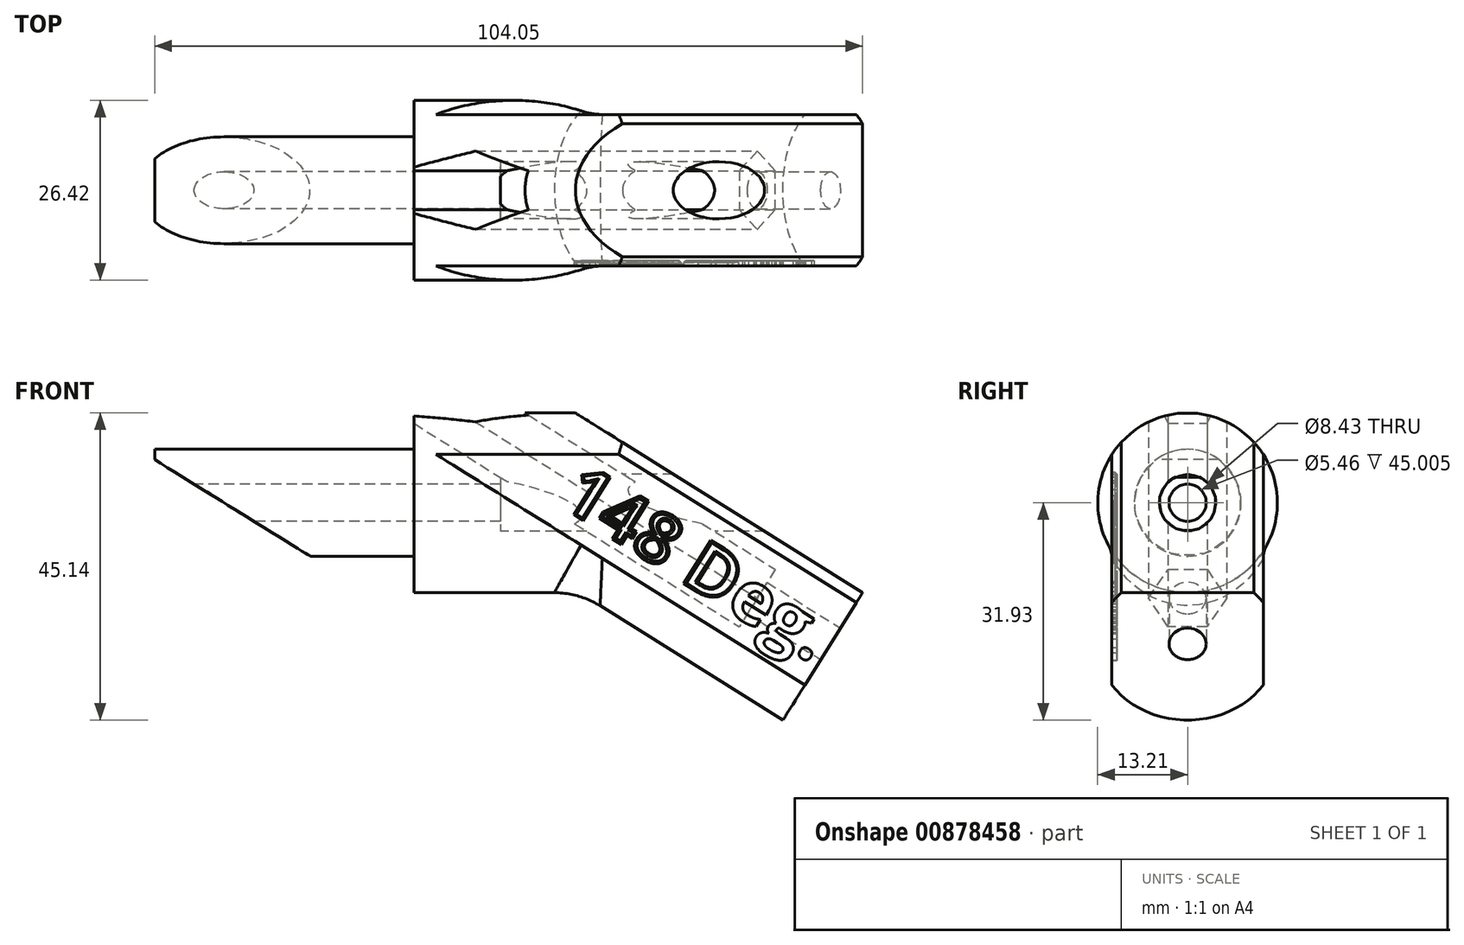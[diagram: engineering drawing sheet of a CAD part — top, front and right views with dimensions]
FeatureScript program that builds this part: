
annotation { "Feature Type Name" : "Feature", "Feature Type Description" : "" }
export const myFeature = defineFeature(function(context is Context, id is Id, definition is map)
    precondition{}
    {
        {
            var Q0;
            Q0=qCreatedBy(makeId("Front.planeOp"),FACE);
            var sketch = newSketch(context, id + "F0", { "sketchPlane" : qUnion([Q0])});
            skLineSegment(sketch, "E0", {"start": v(0, 0) * mm, "end": v(-66.17, 0) * mm});
            skLineSegment(sketch, "E1", {"start": v(0, 0) * mm, "end": v(33.17, -20.73) * mm});
            skSolve(sketch);
        }
        {
            var Q0;
            Q0=sQuery(id+"F0.wireOp",VERTEX,"E0.end");
            var Q1;
            Q1=qCreatedBy(makeId("Right.planeOp"),FACE);
            cPlane(context, id + "F1", {"entities" : qUnion([Q0, Q1]), "cplaneType" : CPlaneType.PLANE_POINT, "offset" : 25.4 * mm, "width" : 152.4 * mm, "height" : 152.4 * mm});
        }
        {
            var Q0;
            Q0=qCreatedBy(id+"F1.planeOp",FACE);
            var sketch = newSketch(context, id + "F2", { "sketchPlane" : qUnion([Q0])});
            skCircle(sketch, "E2", {"center": v(0, 0) * mm, "radius": 13.2 * mm});
            skSolve(sketch);
        }
        {
            var Q0;
            Q0=makeQuery(id+"F2.imprint","IMPRINT",FACE,{"disambiguationData":[TD([[makeQuery(id+"F2.imprint","IMPRINT",EDGE,{"derivedFrom":sQuery(id+"F2.wireOp",EDGE,"E2")}),1.0]])]});
            var Q1;
            Q1=sQuery(id+"F0.wireOp",EDGE,"E0");
            var Q2;
            Q2=sQuery(id+"F0.wireOp",EDGE,"E1");
            sweep(context, id + "F3", {"profiles" : qUnion([Q0]), "path" : qUnion([Q1, Q2])});
        }
        {
            var Q0;
            Q0=makeQuery(id+"F3.opSweep","CAP_FACE",FACE,{"disambiguationData":[OSD([sQuery(id+"F0.wireOp",VERTEX,"E1.end"),sQuery(id+"F2.wireOp",EDGE,"E2")])],"isStart":false});
            var sketch = newSketch(context, id + "F4", { "sketchPlane" : qUnion([Q0])});
            skLineSegment(sketch, "E3", {"start": v(-11.13, 8.9) * mm, "end": v(11.13, 8.9) * mm});
            skLineSegment(sketch, "E4", {"start": v(11.13, 8.9) * mm, "end": v(11.13, -2.08) * mm});
            skLineSegment(sketch, "E5", {"start": v(11.13, -2.08) * mm, "end": v(-11.13, -2.08) * mm, "construction": true});
            skLineSegment(sketch, "E6", {"start": v(-11.13, -2.08) * mm, "end": v(-11.13, 8.89) * mm});
            skPoint(sketch, "E7", {"position": v(0, -13.2) * mm});
            skPoint(sketch, "E8", {"position": v(0, -2.08) * mm});
            skLineSegment(sketch, "E9", {"start": v(11.13, -2.08) * mm, "end": v(11.13, -7.12) * mm});
            skLineSegment(sketch, "E10", {"start": v(11.13, -7.12) * mm, "end": v(17.48, -7.12) * mm});
            skLineSegment(sketch, "E11.bottom", {"start": v(17.48, -7.12) * mm, "end": v(-17.48, -7.12) * mm, "construction": true});
            skLineSegment(sketch, "E11.top", {"start": v(17.48, 30.98) * mm, "end": v(-17.48, 30.98) * mm});
            skLineSegment(sketch, "E11.left", {"start": v(17.48, -7.12) * mm, "end": v(17.48, 30.98) * mm});
            skLineSegment(sketch, "E11.right", {"start": v(-17.48, -7.12) * mm, "end": v(-17.48, 30.98) * mm});
            skLineSegment(sketch, "E12", {"start": v(-11.13, -2.08) * mm, "end": v(-11.13, -7.12) * mm});
            skLineSegment(sketch, "E13", {"start": v(-11.13, -7.12) * mm, "end": v(-17.48, -7.12) * mm});
            skSolve(sketch);
        }
        {
            var Q0;
            Q0=makeQuery(id+"F3.opSweep","CAP_FACE",FACE,{"disambiguationData":[OSD([sQuery(id+"F0.wireOp",VERTEX,"E0.end"),sQuery(id+"F2.wireOp",EDGE,"E2")])],"isStart":true});
            var sketch = newSketch(context, id + "F5", { "sketchPlane" : qUnion([Q0])});
            skCircle(sketch, "E14", {"center": v(0, 0) * mm, "radius": 7.85 * mm});
            skCircle(sketch, "E15", {"center": v(0, 0) * mm, "radius": 19.05 * mm});
            skSolve(sketch);
        }
        {
            var Q0;
            Q0=makeQuery(id+"F5.imprint","IMPRINT",FACE,{"disambiguationData":[TD([[makeQuery(id+"F5.imprint","IMPRINT",EDGE,{"derivedFrom":sQuery(id+"F5.wireOp",EDGE,"E14")}),-1.0]])]});
            extrude(context, id + "F6", {"entities" : qUnion([Q0]), "operationType" : NewBodyOperationType.REMOVE, "oppositeDirection" : true, "depth" : 38.1 * mm, "offsetDistance" : 25.4 * mm});
        }
        {
            var Q0;
            Q0=qCreatedBy(makeId("Front.planeOp"),FACE);
            var sketch = newSketch(context, id + "F7", { "sketchPlane" : qUnion([Q0])});
            skLineSegment(sketch, "E16", {"start": v(-66.17, 6.32) * mm, "end": v(-43.3, -7.85) * mm});
            skLineSegment(sketch, "E17", {"start": v(-43.3, -7.85) * mm, "end": v(-66.17, -7.85) * mm, "construction": true});
            skLineSegment(sketch, "E18", {"start": v(-66.17, -7.85) * mm, "end": v(-66.17, 6.32) * mm});
            skLineSegment(sketch, "E19", {"start": v(-66.17, -7.85) * mm, "end": v(-66.17, -11.02) * mm});
            skLineSegment(sketch, "E20", {"start": v(-66.17, -11.02) * mm, "end": v(-43.3, -11.02) * mm});
            skLineSegment(sketch, "E21", {"start": v(-43.3, -11.02) * mm, "end": v(-43.3, -7.85) * mm});
            skSolve(sketch);
        }
        {
            var Q0;
            Q0 = qSketchRegion(id + "F7", true);
            extrude(context, id + "F8", {"entities" : qUnion([Q0]), "operationType" : NewBodyOperationType.REMOVE, "oppositeDirection" : true, "depth" : 25.4 * mm, "offsetDistance" : 25.4 * mm, "symmetric" : true});
        }
        {
            var Q0;
            Q0=makeQuery(id+"F3.opSweep","CAP_FACE",FACE,{"disambiguationData":[OSD([sQuery(id+"F0.wireOp",VERTEX,"E0.end"),sQuery(id+"F2.wireOp",EDGE,"E2")])],"isStart":true});
            var sketch = newSketch(context, id + "F9", { "sketchPlane" : qUnion([Q0])});
            skCircle(sketch, "E22", {"center": v(0, 0) * mm, "radius": 2.73 * mm});
            skSolve(sketch);
        }
        {
            var Q0;
            Q0 = qSketchRegion(id + "F9", true);
            extrude(context, id + "F10", {"entities" : qUnion([Q0]), "operationType" : NewBodyOperationType.REMOVE, "endBound" : BoundingType.THROUGH_ALL, "oppositeDirection" : true, "depth" : 25.4 * mm, "offsetDistance" : 25.4 * mm});
        }
        {
            var Q0;
            Q0=makeQuery(id+"F6.boolean.opBoolean","COPY",FACE,{"derivedFrom":makeQuery(id+"F6.opExtrude","CAP_FACE",FACE,{"disambiguationData":[OSD([sQuery(id+"F0.wireOp",VERTEX,"E0.end"),sQuery(id+"F2.wireOp",EDGE,"E2"),sQuery(id+"F5.wireOp",EDGE,"E14")])],"isStart":false})});
            cPlane(context, id + "F11", {"entities" : qUnion([Q0]), "cplaneType" : CPlaneType.OFFSET, "offset" : 12.7 * mm, "oppositeDirection" : true, "width" : 152.4 * mm, "height" : 152.4 * mm});
        }
        {
            var Q0;
            Q0=qCreatedBy(id+"F11.planeOp",FACE);
            var sketch = newSketch(context, id + "F12", { "sketchPlane" : qUnion([Q0])});
            skCircle(sketch, "E23", {"center": v(0, 0) * mm, "radius": 4.22 * mm});
            skSolve(sketch);
        }
        {
            var Q0;
            Q0 = qSketchRegion(id + "F12", true);
            extrude(context, id + "F13", {"entities" : qUnion([Q0]), "operationType" : NewBodyOperationType.REMOVE, "endBound" : BoundingType.THROUGH_ALL, "oppositeDirection" : true, "depth" : 25.4 * mm, "offsetDistance" : 25.4 * mm});
        }
        {
            var Q0;
            Q0 = qSketchRegion(id + "F4", true);
            var Q1;
            Q1 = qConstructionFilter(qBodyType(qCreatedBy(id + "F4" ,EDGE), BodyType.WIRE), ConstructionObject.NO);
            extrude(context, id + "F14", {"entities" : qUnion([Q0]), "operationType" : NewBodyOperationType.REMOVE, "surfaceEntities" : qUnion([Q1]), "endBound" : BoundingType.THROUGH_ALL, "oppositeDirection" : true, "depth" : 25.4 * mm, "offsetDistance" : 25.4 * mm});
        }
        {
            var Q0;
            Q0=makeQuery(id+"F3.opSweep","CAP_FACE",FACE,{"disambiguationData":[OSD([sQuery(id+"F0.wireOp",VERTEX,"E1.end"),sQuery(id+"F2.wireOp",EDGE,"E2")])],"isStart":false});
            var sketch = newSketch(context, id + "F15", { "sketchPlane" : qUnion([Q0])});
            skCircle(sketch, "E24", {"center": v(0, 0) * mm, "radius": 2.73 * mm});
            skSolve(sketch);
        }
        {
            var Q0;
            Q0 = qSketchRegion(id + "F15", true);
            extrude(context, id + "F16", {"entities" : qUnion([Q0]), "operationType" : NewBodyOperationType.REMOVE, "endBound" : BoundingType.THROUGH_ALL, "oppositeDirection" : true, "depth" : 25.4 * mm, "offsetDistance" : 25.4 * mm});
        }
        {
            var Q0;
            Q0=makeQuery(id+"F3.opSweep","CAP_FACE",FACE,{"disambiguationData":[OSD([sQuery(id+"F0.wireOp",VERTEX,"E1.end"),sQuery(id+"F2.wireOp",EDGE,"E2")])],"isStart":false});
            cPlane(context, id + "F17", {"entities" : qUnion([Q0]), "cplaneType" : CPlaneType.OFFSET, "offset" : 12.7 * mm, "oppositeDirection" : true, "width" : 152.4 * mm, "height" : 152.4 * mm});
        }
        {
            var Q0;
            Q0=qCreatedBy(id+"F17.planeOp",FACE);
            var sketch = newSketch(context, id + "F18", { "sketchPlane" : qUnion([Q0])});
            skCircle(sketch, "E25.cCircle", {"center": v(0, 0) * mm, "radius": 4.98 * mm, "construction": true});
            skLineSegment(sketch, "E25.0", {"start": v(2.87, -4.98) * mm, "end": v(-2.87, -4.98) * mm});
            skLineSegment(sketch, "E25.1", {"start": v(-2.87, -4.98) * mm, "end": v(-5.75, 0) * mm});
            skLineSegment(sketch, "E25.2", {"start": v(-5.75, 0) * mm, "end": v(-2.87, 4.98) * mm});
            skLineSegment(sketch, "E25.3", {"start": v(-2.87, 4.98) * mm, "end": v(2.87, 4.98) * mm});
            skLineSegment(sketch, "E25.4", {"start": v(2.87, 4.98) * mm, "end": v(5.75, 0) * mm});
            skLineSegment(sketch, "E25.5", {"start": v(5.75, 0) * mm, "end": v(2.87, -4.98) * mm});
            skPoint(sketch, "E25.0.midPoint", {"position": v(0, -4.98) * mm});
            skSolve(sketch);
        }
        {
            var Q0;
            Q0 = qSketchRegion(id + "F18", true);
            extrude(context, id + "F19", {"entities" : qUnion([Q0]), "operationType" : NewBodyOperationType.REMOVE, "endBound" : BoundingType.THROUGH_ALL, "oppositeDirection" : true, "depth" : 25.4 * mm, "offsetDistance" : 25.4 * mm});
        }
        {
            var Q0;
            {var subQ0=sQuery(id+"F2.wireOp",EDGE,"E2");Q0=makeQuery(id+"F14.boolean.opBoolean","SPLIT",EDGE,{"disambiguationData":[TD([makeQuery(id+"F3.opSweep","SWEPT_FACE",FACE,{"disambiguationData":[OSD([sQuery(id+"F0.wireOp",EDGE,"E0"),subQ0])]}),makeQuery(id+"F3.opSweep","SWEPT_FACE",FACE,{"disambiguationData":[OSD([sQuery(id+"F0.wireOp",EDGE,"E1"),subQ0])]}),makeQuery(id+"F14.opExtrude","SWEPT_FACE",FACE,{"disambiguationData":[OSD([sQuery(id+"F4.wireOp",EDGE,"E4"),sQuery(id+"F4.wireOp",EDGE,"E9")])]}),makeQuery(id+"F14.opExtrude","SWEPT_FACE",FACE,{"disambiguationData":[OSD([sQuery(id+"F4.wireOp",EDGE,"E6"),sQuery(id+"F4.wireOp",EDGE,"E12")])]}),makeQuery(id+"F14.opExtrude","SWEPT_FACE",FACE,{"disambiguationData":[OSD([sQuery(id+"F4.wireOp",EDGE,"E10")])]}),makeQuery(id+"F14.opExtrude","SWEPT_FACE",FACE,{"disambiguationData":[OSD([sQuery(id+"F4.wireOp",EDGE,"E13")])]})])],"derivedFrom":makeQuery(id+"F3.opSweep","MID_CAP_EDGE",EDGE,{"disambiguationData":[OSD([sQuery(id+"F0.wireOp",VERTEX,"E1.start"),subQ0])],"capPos":1.0})});}
            fillet(context, id + "F20", {"entities" : qUnion([Q0]), "radius" : 12.7 * mm, "tangentPropagation" : true, "allowEdgeOverflow" : false});
        }
        {
            var Q0;
            Q0=makeQuery(id+"F14.boolean.opBoolean","COPY",FACE,{"derivedFrom":makeQuery(id+"F14.opExtrude","SWEPT_FACE",FACE,{"disambiguationData":[OSD([sQuery(id+"F4.wireOp",EDGE,"E6"),sQuery(id+"F4.wireOp",EDGE,"E12")])]})});
            var sketch = newSketch(context, id + "F21", { "sketchPlane" : qUnion([Q0])});
            skText(sketch, "E26", { "text": "148 Deg.", "fontName": "OpenSans-Bold.ttf"});
            const initialGuessF21  = {"E26": [-0.00691, -0.00033, 0.84805, -0.52992, 0.00762]};
            skSetInitialGuess(sketch, initialGuessF21);
            skSolve(sketch);
        }
        {
            var Q0;
            Q0 = qSketchRegion(id + "F21", true);
            extrude(context, id + "F22", {"entities" : qUnion([Q0]), "operationType" : NewBodyOperationType.REMOVE, "oppositeDirection" : true, "depth" : 0.76 * mm, "offsetDistance" : 25.4 * mm});
        }
        {
            var Q0;
            Q0=makeQuery(id+"F22.boolean.opBoolean","COPY",FACE,{"derivedFrom":makeQuery(id+"F22.opExtrude","CAP_FACE",FACE,{"disambiguationData":[OSD([sQuery(id+"F21.wireOp",EDGE,"E26.sketch_text.stroke-60"),sQuery(id+"F21.wireOp",EDGE,"E26.sketch_text.stroke-61"),sQuery(id+"F21.wireOp",EDGE,"E26.sketch_text.stroke-62"),sQuery(id+"F21.wireOp",EDGE,"E26.sketch_text.stroke-63"),sQuery(id+"F21.wireOp",EDGE,"E26.sketch_text.stroke-64"),sQuery(id+"F21.wireOp",EDGE,"E26.sketch_text.stroke-65"),sQuery(id+"F21.wireOp",EDGE,"E26.sketch_text.stroke-66"),sQuery(id+"F21.wireOp",EDGE,"E26.sketch_text.stroke-67"),sQuery(id+"F21.wireOp",EDGE,"E26.sketch_text.stroke-68"),sQuery(id+"F21.wireOp",EDGE,"E26.sketch_text.stroke-69"),sQuery(id+"F21.wireOp",EDGE,"E26.sketch_text.stroke-70"),sQuery(id+"F21.wireOp",EDGE,"E26.sketch_text.stroke-71"),sQuery(id+"F21.wireOp",EDGE,"E26.sketch_text.stroke-72"),sQuery(id+"F21.wireOp",EDGE,"E26.sketch_text.stroke-73"),sQuery(id+"F21.wireOp",EDGE,"E26.sketch_text.stroke-74"),sQuery(id+"F21.wireOp",EDGE,"E26.sketch_text.stroke-75"),sQuery(id+"F21.wireOp",EDGE,"E26.sketch_text.stroke-76"),sQuery(id+"F21.wireOp",EDGE,"E26.sketch_text.stroke-77"),sQuery(id+"F21.wireOp",EDGE,"E26.sketch_text.stroke-78"),sQuery(id+"F21.wireOp",EDGE,"E26.sketch_text.stroke-79")])],"isStart":false})});
            var Q1;
            Q1=makeQuery(id+"F22.boolean.opBoolean","COPY",FACE,{"derivedFrom":makeQuery(id+"F22.opExtrude","CAP_FACE",FACE,{"disambiguationData":[OSD([sQuery(id+"F21.wireOp",EDGE,"E26.sketch_text.stroke-124"),sQuery(id+"F21.wireOp",EDGE,"E26.sketch_text.stroke-125"),sQuery(id+"F21.wireOp",EDGE,"E26.sketch_text.stroke-126"),sQuery(id+"F21.wireOp",EDGE,"E26.sketch_text.stroke-127"),sQuery(id+"F21.wireOp",EDGE,"E26.sketch_text.stroke-128"),sQuery(id+"F21.wireOp",EDGE,"E26.sketch_text.stroke-129"),sQuery(id+"F21.wireOp",EDGE,"E26.sketch_text.stroke-130"),sQuery(id+"F21.wireOp",EDGE,"E26.sketch_text.stroke-131")])],"isStart":false})});
            var Q2;
            Q2=makeQuery(id+"F22.boolean.opBoolean","COPY",FACE,{"derivedFrom":makeQuery(id+"F22.opExtrude","CAP_FACE",FACE,{"disambiguationData":[OSD([sQuery(id+"F21.wireOp",EDGE,"E26.sketch_text.stroke-0"),sQuery(id+"F21.wireOp",EDGE,"E26.sketch_text.stroke-1"),sQuery(id+"F21.wireOp",EDGE,"E26.sketch_text.stroke-2"),sQuery(id+"F21.wireOp",EDGE,"E26.sketch_text.stroke-3"),sQuery(id+"F21.wireOp",EDGE,"E26.sketch_text.stroke-4"),sQuery(id+"F21.wireOp",EDGE,"E26.sketch_text.stroke-5"),sQuery(id+"F21.wireOp",EDGE,"E26.sketch_text.stroke-6"),sQuery(id+"F21.wireOp",EDGE,"E26.sketch_text.stroke-7"),sQuery(id+"F21.wireOp",EDGE,"E26.sketch_text.stroke-8"),sQuery(id+"F21.wireOp",EDGE,"E26.sketch_text.stroke-9")])],"isStart":false})});
            chamfer(context, id + "F23", {"entities" : qUnion([Q0, Q1, Q2]), "width" : 0.25 * mm, "tangentPropagation" : true});
        }
        {
            var Q0;
            Q0=makeQuery(id+"F22.boolean.opBoolean","COPY",FACE,{"derivedFrom":makeQuery(id+"F22.opExtrude","CAP_FACE",FACE,{"disambiguationData":[OSD([sQuery(id+"F21.wireOp",EDGE,"E26.sketch_text.stroke-10"),sQuery(id+"F21.wireOp",EDGE,"E26.sketch_text.stroke-11"),sQuery(id+"F21.wireOp",EDGE,"E26.sketch_text.stroke-12"),sQuery(id+"F21.wireOp",EDGE,"E26.sketch_text.stroke-13"),sQuery(id+"F21.wireOp",EDGE,"E26.sketch_text.stroke-14"),sQuery(id+"F21.wireOp",EDGE,"E26.sketch_text.stroke-15"),sQuery(id+"F21.wireOp",EDGE,"E26.sketch_text.stroke-16"),sQuery(id+"F21.wireOp",EDGE,"E26.sketch_text.stroke-17"),sQuery(id+"F21.wireOp",EDGE,"E26.sketch_text.stroke-18"),sQuery(id+"F21.wireOp",EDGE,"E26.sketch_text.stroke-19"),sQuery(id+"F21.wireOp",EDGE,"E26.sketch_text.stroke-20"),sQuery(id+"F21.wireOp",EDGE,"E26.sketch_text.stroke-21"),sQuery(id+"F21.wireOp",EDGE,"E26.sketch_text.stroke-22"),sQuery(id+"F21.wireOp",EDGE,"E26.sketch_text.stroke-23"),sQuery(id+"F21.wireOp",EDGE,"E26.sketch_text.stroke-24"),sQuery(id+"F21.wireOp",EDGE,"E26.sketch_text.stroke-25"),sQuery(id+"F21.wireOp",EDGE,"E26.sketch_text.stroke-26"),sQuery(id+"F21.wireOp",EDGE,"E26.sketch_text.stroke-27")])],"isStart":false})});
            var Q1;
            Q1=makeQuery(id+"F22.boolean.opBoolean","COPY",FACE,{"derivedFrom":makeQuery(id+"F22.opExtrude","CAP_FACE",FACE,{"disambiguationData":[OSD([sQuery(id+"F21.wireOp",EDGE,"E26.sketch_text.stroke-28"),sQuery(id+"F21.wireOp",EDGE,"E26.sketch_text.stroke-29"),sQuery(id+"F21.wireOp",EDGE,"E26.sketch_text.stroke-30"),sQuery(id+"F21.wireOp",EDGE,"E26.sketch_text.stroke-31"),sQuery(id+"F21.wireOp",EDGE,"E26.sketch_text.stroke-32"),sQuery(id+"F21.wireOp",EDGE,"E26.sketch_text.stroke-33"),sQuery(id+"F21.wireOp",EDGE,"E26.sketch_text.stroke-34"),sQuery(id+"F21.wireOp",EDGE,"E26.sketch_text.stroke-35"),sQuery(id+"F21.wireOp",EDGE,"E26.sketch_text.stroke-36"),sQuery(id+"F21.wireOp",EDGE,"E26.sketch_text.stroke-37"),sQuery(id+"F21.wireOp",EDGE,"E26.sketch_text.stroke-38"),sQuery(id+"F21.wireOp",EDGE,"E26.sketch_text.stroke-39"),sQuery(id+"F21.wireOp",EDGE,"E26.sketch_text.stroke-40"),sQuery(id+"F21.wireOp",EDGE,"E26.sketch_text.stroke-41"),sQuery(id+"F21.wireOp",EDGE,"E26.sketch_text.stroke-42"),sQuery(id+"F21.wireOp",EDGE,"E26.sketch_text.stroke-43"),sQuery(id+"F21.wireOp",EDGE,"E26.sketch_text.stroke-44"),sQuery(id+"F21.wireOp",EDGE,"E26.sketch_text.stroke-45")])],"isStart":false})});
            chamfer(context, id + "F24", {"entities" : qUnion([Q0, Q1]), "width" : 0.38 * mm, "tangentPropagation" : true});
        }
    });
